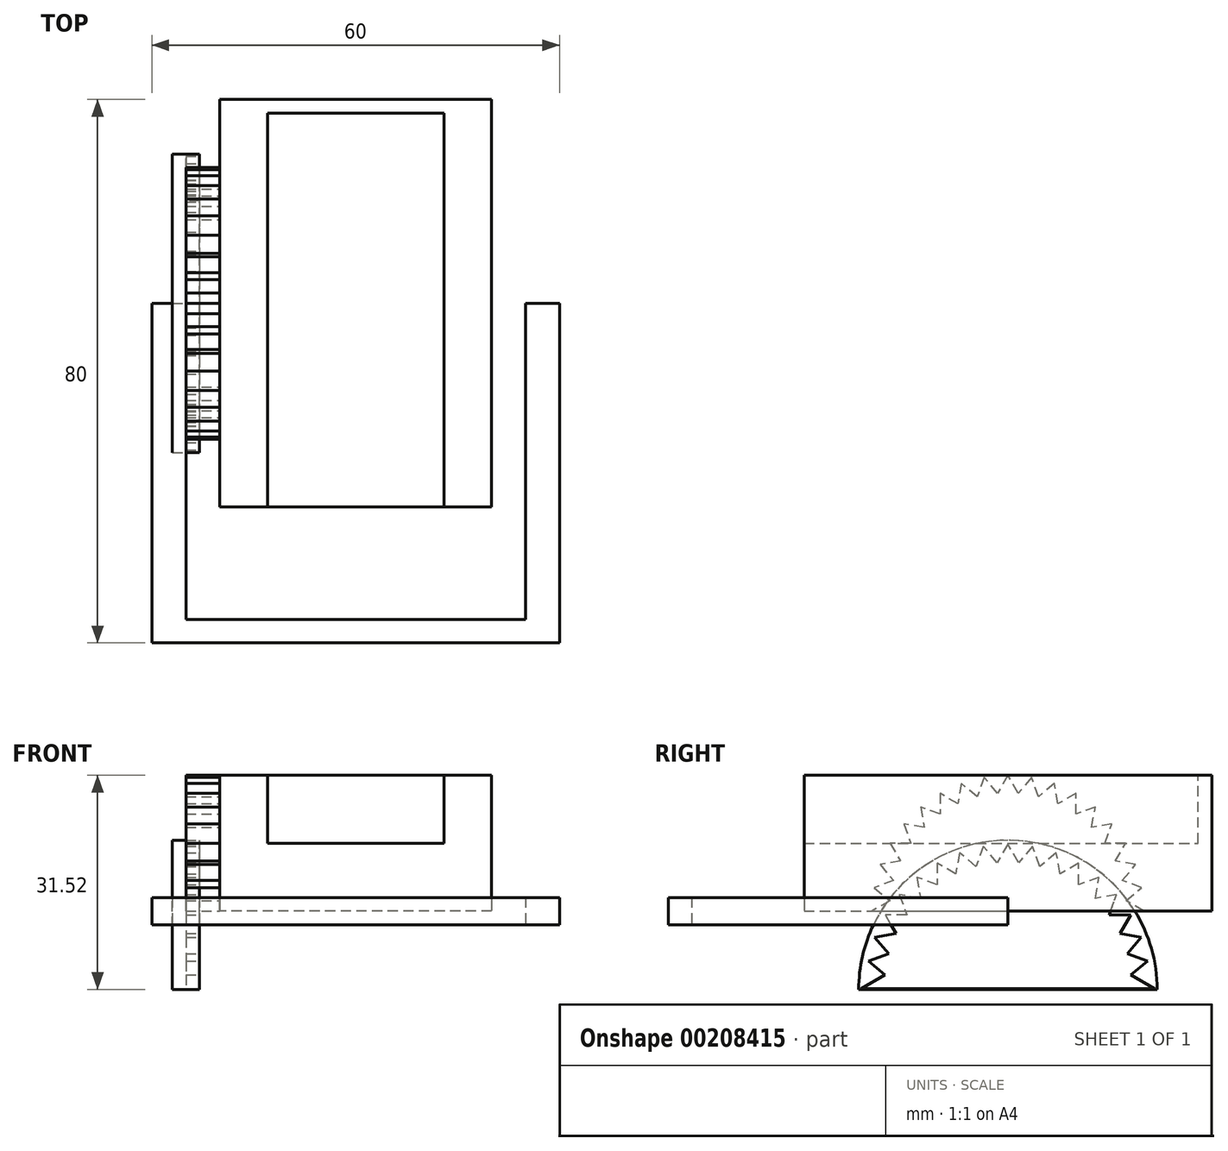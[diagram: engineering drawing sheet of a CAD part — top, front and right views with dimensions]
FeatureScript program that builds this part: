
annotation { "Feature Type Name" : "Feature", "Feature Type Description" : "" }
export const myFeature = defineFeature(function(context is Context, id is Id, definition is map)
    precondition{}
    {
        {
            var Q0;
            Q0=qCreatedBy(makeId("Top.planeOp"),FACE);
            var sketch = newSketch(context, id + "F0", { "sketchPlane" : qUnion([Q0])});
            skLineSegment(sketch, "E0.bottom", {"start": v(-20, -30) * mm, "end": v(20, -30) * mm});
            skLineSegment(sketch, "E0.top", {"start": v(-20, 30) * mm, "end": v(20, 30) * mm});
            skLineSegment(sketch, "E0.left", {"start": v(-20, -30) * mm, "end": v(-20, 30) * mm});
            skLineSegment(sketch, "E0.right", {"start": v(20, -30) * mm, "end": v(20, 30) * mm});
            skSolve(sketch);
        }
        {
            var Q0;
            Q0=qSketchRegion(id+"F0",true);
            extrude(context, id + "F1", {"entities" : qUnion([Q0]), "depth" : 20 * mm});
        }
        {
            var Q0;
            Q0=makeQuery(id+"F1.opExtrude","CAP_FACE",FACE,{"disambiguationData":[OSD([sQuery(id+"F0.wireOp",EDGE,"E0.bottom"),sQuery(id+"F0.wireOp",EDGE,"E0.top"),sQuery(id+"F0.wireOp",EDGE,"E0.left"),sQuery(id+"F0.wireOp",EDGE,"E0.right")])],"isStart":false});
            var sketch = newSketch(context, id + "F2", { "sketchPlane" : qUnion([Q0])});
            skLineSegment(sketch, "E1.top", {"start": v(-13, 28) * mm, "end": v(13, 28) * mm});
            skLineSegment(sketch, "E1.left", {"start": v(-13, -32) * mm, "end": v(-13, 28) * mm});
            skLineSegment(sketch, "E1.right", {"start": v(13, -32) * mm, "end": v(13, 28) * mm});
            skLineSegment(sketch, "E2", {"start": v(13, -32) * mm, "end": v(-13, -32) * mm});
            skSolve(sketch);
        }
        {
            var Q0;
            Q0=makeQuery(id+"F2.imprint","IMPRINT",FACE,{"disambiguationData":[TD([[makeQuery(id+"F2.imprint","IMPRINT",EDGE,{"derivedFrom":sQuery(id+"F2.wireOp",EDGE,"E1.top")}),-1.0]])]});
            extrude(context, id + "F3", {"entities" : qUnion([Q0]), "operationType" : NewBodyOperationType.REMOVE, "oppositeDirection" : true, "depth" : 10 * mm});
        }
        {
            var Q0;
            Q0=makeQuery(id+"F1.opExtrude","SWEPT_FACE",FACE,{"disambiguationData":[OSD([sQuery(id+"F0.wireOp",EDGE,"E0.right")])]});
            var sketch = newSketch(context, id + "F4", { "sketchPlane" : qUnion([Q0])});
            skPoint(sketch, "E3.center", {"position": v(0, 0) * mm});
            skLineSegment(sketch, "E4", {"start": v(7.37, 15.8) * mm, "end": v(6.84, 18.8) * mm});
            skLineSegment(sketch, "E5", {"start": v(6.84, 18.8) * mm, "end": v(4.51, 16.84) * mm});
            skLineSegment(sketch, "E6.1.0", {"start": v(4.51, 16.84) * mm, "end": v(3.47, 19.7) * mm});
            skLineSegment(sketch, "E6.1.1", {"start": v(3.47, 19.7) * mm, "end": v(1.52, 17.37) * mm});
            skLineSegment(sketch, "E6.2.0", {"start": v(1.52, 17.37) * mm, "end": v(0, 20) * mm});
            skLineSegment(sketch, "E6.2.1", {"start": v(0, 20) * mm, "end": v(-1.52, 17.37) * mm});
            skLineSegment(sketch, "E6.3.0", {"start": v(-1.52, 17.37) * mm, "end": v(-3.47, 19.7) * mm});
            skLineSegment(sketch, "E6.3.1", {"start": v(-3.47, 19.7) * mm, "end": v(-4.51, 16.84) * mm});
            skLineSegment(sketch, "E6.4.0", {"start": v(-4.51, 16.84) * mm, "end": v(-6.84, 18.8) * mm});
            skLineSegment(sketch, "E6.4.1", {"start": v(-6.84, 18.8) * mm, "end": v(-7.37, 15.8) * mm});
            skLineSegment(sketch, "E6.5.0", {"start": v(-7.37, 15.8) * mm, "end": v(-10, 17.32) * mm});
            skLineSegment(sketch, "E6.5.1", {"start": v(-10, 17.32) * mm, "end": v(-10, 14.28) * mm});
            skLineSegment(sketch, "E6.6.0", {"start": v(-10, 14.28) * mm, "end": v(-12.86, 15.32) * mm});
            skLineSegment(sketch, "E6.6.1", {"start": v(-12.86, 15.32) * mm, "end": v(-12.33, 12.33) * mm});
            skLineSegment(sketch, "E6.7.0", {"start": v(-12.33, 12.33) * mm, "end": v(-15.32, 12.86) * mm});
            skLineSegment(sketch, "E6.7.1", {"start": v(-15.32, 12.86) * mm, "end": v(-14.28, 10) * mm});
            skLineSegment(sketch, "E6.8.0", {"start": v(-14.28, 10) * mm, "end": v(-17.32, 10) * mm});
            skLineSegment(sketch, "E6.8.1", {"start": v(-17.32, 10) * mm, "end": v(-15.8, 7.37) * mm});
            skLineSegment(sketch, "E6.9.0", {"start": v(-15.8, 7.37) * mm, "end": v(-18.8, 6.84) * mm});
            skLineSegment(sketch, "E6.9.1", {"start": v(-18.8, 6.84) * mm, "end": v(-16.84, 4.51) * mm});
            skLineSegment(sketch, "E6.10.0", {"start": v(-16.84, 4.51) * mm, "end": v(-19.7, 3.47) * mm});
            skLineSegment(sketch, "E6.10.1", {"start": v(-19.7, 3.47) * mm, "end": v(-17.37, 1.52) * mm});
            skLineSegment(sketch, "E6.11.0", {"start": v(-17.37, 1.52) * mm, "end": v(-20, 0) * mm});
            skLineSegment(sketch, "E6.29.1", {"start": v(20, 0) * mm, "end": v(17.37, 1.52) * mm});
            skLineSegment(sketch, "E6.30.0", {"start": v(17.37, 1.52) * mm, "end": v(19.7, 3.47) * mm});
            skLineSegment(sketch, "E6.30.1", {"start": v(19.7, 3.47) * mm, "end": v(16.84, 4.51) * mm});
            skLineSegment(sketch, "E6.31.0", {"start": v(16.84, 4.51) * mm, "end": v(18.8, 6.84) * mm});
            skLineSegment(sketch, "E6.31.1", {"start": v(18.8, 6.84) * mm, "end": v(15.8, 7.37) * mm});
            skLineSegment(sketch, "E6.32.0", {"start": v(15.8, 7.37) * mm, "end": v(17.32, 10) * mm});
            skLineSegment(sketch, "E6.32.1", {"start": v(17.32, 10) * mm, "end": v(14.28, 10) * mm});
            skLineSegment(sketch, "E6.33.0", {"start": v(14.28, 10) * mm, "end": v(15.32, 12.86) * mm});
            skLineSegment(sketch, "E6.33.1", {"start": v(15.32, 12.86) * mm, "end": v(12.33, 12.33) * mm});
            skLineSegment(sketch, "E6.34.0", {"start": v(12.33, 12.33) * mm, "end": v(12.86, 15.32) * mm});
            skLineSegment(sketch, "E6.34.1", {"start": v(12.86, 15.32) * mm, "end": v(10, 14.28) * mm});
            skLineSegment(sketch, "E6.35.0", {"start": v(10, 14.28) * mm, "end": v(10, 17.32) * mm});
            skLineSegment(sketch, "E6.35.1", {"start": v(10, 17.32) * mm, "end": v(7.37, 15.8) * mm});
            skLineSegment(sketch, "E7", {"start": v(20, 0) * mm, "end": v(-20, 0) * mm});
            skSolve(sketch);
        }
        {
            var Q0;
            Q0=makeQuery(id+"F4.imprint","IMPRINT",FACE,{"disambiguationData":[TD([[makeQuery(id+"F4.imprint","IMPRINT",EDGE,{"derivedFrom":sQuery(id+"F4.wireOp",EDGE,"E4")}),1.0]])]});
            extrude(context, id + "F5", {"entities" : qUnion([Q0]), "operationType" : NewBodyOperationType.ADD, "depth" : 5 * mm});
        }
        {
            var Q0;
            Q0=makeQuery(id+"F1.opExtrude","SWEPT_BODY",BODY,{"disambiguationData":[OSD([sQuery(id+"F0.wireOp",EDGE,"E0.bottom"),sQuery(id+"F0.wireOp",EDGE,"E0.top"),sQuery(id+"F0.wireOp",EDGE,"E0.left"),sQuery(id+"F0.wireOp",EDGE,"E0.right")])]});
            var Q1;
            Q1=qCreatedBy(makeId("Right.planeOp"),FACE);
            mirror(context, id + "F6", {"entities" : qUnion([Q0]), "mirrorPlane" : qUnion([Q1])});
        }
        {
            var Q0;
            Q0=qCreatedBy(makeId("Right.planeOp"),FACE);
            cPlane(context, id + "F7", {"entities" : qUnion([Q0]), "cplaneType" : CPlaneType.OFFSET, "offset" : 23 * mm, "width" : 152.4 * mm, "height" : 152.4 * mm});
        }
        {
            var Q0;
            Q0=qCreatedBy(makeId("Right.planeOp"),FACE);
            cPlane(context, id + "F8", {"entities" : qUnion([Q0]), "cplaneType" : CPlaneType.OFFSET, "offset" : 23 * mm, "oppositeDirection" : true, "width" : 152.4 * mm, "height" : 152.4 * mm});
        }
        {
            var Q0;
            Q0=qCreatedBy(id+"F8.planeOp",FACE);
            var sketch = newSketch(context, id + "F9", { "sketchPlane" : qUnion([Q0])});
            skPoint(sketch, "E8.center", {"position": v(0, -11) * mm});
            skLineSegment(sketch, "E9", {"start": v(7.37, 4.81) * mm, "end": v(6.84, 7.8) * mm});
            skLineSegment(sketch, "E10", {"start": v(6.84, 7.8) * mm, "end": v(4.51, 5.85) * mm});
            skLineSegment(sketch, "E11.1.0", {"start": v(4.51, 5.85) * mm, "end": v(3.47, 8.7) * mm});
            skLineSegment(sketch, "E11.1.1", {"start": v(3.47, 8.7) * mm, "end": v(1.52, 6.38) * mm});
            skLineSegment(sketch, "E11.2.0", {"start": v(1.52, 6.38) * mm, "end": v(0, 9) * mm});
            skLineSegment(sketch, "E11.2.1", {"start": v(0, 9) * mm, "end": v(-1.52, 6.38) * mm});
            skLineSegment(sketch, "E11.3.0", {"start": v(-1.52, 6.38) * mm, "end": v(-3.47, 8.7) * mm});
            skLineSegment(sketch, "E11.3.1", {"start": v(-3.47, 8.7) * mm, "end": v(-4.51, 5.85) * mm});
            skLineSegment(sketch, "E11.4.0", {"start": v(-4.51, 5.85) * mm, "end": v(-6.84, 7.8) * mm});
            skLineSegment(sketch, "E11.4.1", {"start": v(-6.84, 7.8) * mm, "end": v(-7.37, 4.81) * mm});
            skLineSegment(sketch, "E11.5.0", {"start": v(-7.37, 4.81) * mm, "end": v(-10, 6.33) * mm});
            skLineSegment(sketch, "E11.5.1", {"start": v(-10, 6.33) * mm, "end": v(-10, 3.3) * mm});
            skLineSegment(sketch, "E11.6.0", {"start": v(-10, 3.3) * mm, "end": v(-12.86, 4.33) * mm});
            skLineSegment(sketch, "E11.6.1", {"start": v(-12.86, 4.33) * mm, "end": v(-12.33, 1.34) * mm});
            skLineSegment(sketch, "E11.7.0", {"start": v(-12.33, 1.34) * mm, "end": v(-15.32, 1.87) * mm});
            skLineSegment(sketch, "E11.7.1", {"start": v(-15.32, 1.87) * mm, "end": v(-14.28, -1) * mm});
            skLineSegment(sketch, "E11.8.0", {"start": v(-14.28, -1) * mm, "end": v(-17.32, -1) * mm});
            skLineSegment(sketch, "E11.8.1", {"start": v(-17.32, -1) * mm, "end": v(-15.8, -3.62) * mm});
            skLineSegment(sketch, "E11.9.0", {"start": v(-15.8, -3.62) * mm, "end": v(-18.8, -4.15) * mm});
            skLineSegment(sketch, "E11.9.1", {"start": v(-18.8, -4.15) * mm, "end": v(-16.84, -6.48) * mm});
            skLineSegment(sketch, "E11.10.0", {"start": v(-16.84, -6.48) * mm, "end": v(-19.7, -7.52) * mm});
            skLineSegment(sketch, "E11.10.1", {"start": v(-19.7, -7.52) * mm, "end": v(-17.37, -9.47) * mm});
            skLineSegment(sketch, "E11.11.0", {"start": v(-17.37, -9.47) * mm, "end": v(-20, -11) * mm});
            skLineSegment(sketch, "E11.29.1", {"start": v(20, -11) * mm, "end": v(17.37, -9.47) * mm});
            skLineSegment(sketch, "E11.30.0", {"start": v(17.37, -9.47) * mm, "end": v(19.7, -7.52) * mm});
            skLineSegment(sketch, "E11.30.1", {"start": v(19.7, -7.52) * mm, "end": v(16.84, -6.48) * mm});
            skLineSegment(sketch, "E11.31.0", {"start": v(16.84, -6.48) * mm, "end": v(18.8, -4.15) * mm});
            skLineSegment(sketch, "E11.31.1", {"start": v(18.8, -4.15) * mm, "end": v(15.8, -3.62) * mm});
            skLineSegment(sketch, "E11.32.0", {"start": v(15.8, -3.62) * mm, "end": v(17.32, -1) * mm});
            skLineSegment(sketch, "E11.32.1", {"start": v(17.32, -1) * mm, "end": v(14.28, -1) * mm});
            skLineSegment(sketch, "E11.33.0", {"start": v(14.28, -1) * mm, "end": v(15.32, 1.87) * mm});
            skLineSegment(sketch, "E11.33.1", {"start": v(15.32, 1.87) * mm, "end": v(12.33, 1.34) * mm});
            skLineSegment(sketch, "E11.34.0", {"start": v(12.33, 1.34) * mm, "end": v(12.86, 4.33) * mm});
            skLineSegment(sketch, "E11.34.1", {"start": v(12.86, 4.33) * mm, "end": v(10, 3.3) * mm});
            skLineSegment(sketch, "E11.35.0", {"start": v(10, 3.3) * mm, "end": v(10, 6.33) * mm});
            skLineSegment(sketch, "E11.35.1", {"start": v(10, 6.33) * mm, "end": v(7.37, 4.81) * mm});
            skLineSegment(sketch, "E12", {"start": v(20, -11) * mm, "end": v(-20, -11) * mm});
            skSolve(sketch);
        }
        {
            var Q0;
            Q0=qCreatedBy(id+"F8.planeOp",FACE);
            var sketch = newSketch(context, id + "F10", { "sketchPlane" : qUnion([Q0])});
            skLineSegment(sketch, "E13.0", {"start": v(10.43, 3.9) * mm, "end": v(10.43, 7.08) * mm});
            skLineSegment(sketch, "E13.1", {"start": v(13.41, 5) * mm, "end": v(10.43, 3.9) * mm});
            skLineSegment(sketch, "E13.2", {"start": v(12.86, 1.87) * mm, "end": v(13.41, 5) * mm});
            skLineSegment(sketch, "E13.3", {"start": v(15.98, 2.42) * mm, "end": v(12.86, 1.87) * mm});
            skLineSegment(sketch, "E13.4", {"start": v(14.9, -0.56) * mm, "end": v(15.98, 2.42) * mm});
            skLineSegment(sketch, "E13.5", {"start": v(18.07, -0.56) * mm, "end": v(14.9, -0.56) * mm});
            skLineSegment(sketch, "E13.6", {"start": v(16.48, -3.3) * mm, "end": v(18.07, -0.56) * mm});
            skLineSegment(sketch, "E13.7", {"start": v(19.6, -3.85) * mm, "end": v(16.48, -3.3) * mm});
            skLineSegment(sketch, "E13.8", {"start": v(17.57, -6.28) * mm, "end": v(19.6, -3.85) * mm});
            skLineSegment(sketch, "E13.9", {"start": v(20.55, -7.37) * mm, "end": v(17.57, -6.28) * mm});
            skLineSegment(sketch, "E13.10", {"start": v(18.12, -9.4) * mm, "end": v(20.55, -7.37) * mm});
            skLineSegment(sketch, "E13.11", {"start": v(10.43, 7.08) * mm, "end": v(7.69, 5.5) * mm});
            skLineSegment(sketch, "E13.12", {"start": v(21.61, -11.42) * mm, "end": v(18.12, -9.4) * mm});
            skLineSegment(sketch, "E13.13", {"start": v(-21.61, -11.42) * mm, "end": v(21.61, -11.42) * mm});
            skLineSegment(sketch, "E13.14", {"start": v(-18.12, -9.4) * mm, "end": v(-21.61, -11.42) * mm});
            skLineSegment(sketch, "E13.15", {"start": v(-7.14, 8.61) * mm, "end": v(-7.69, 5.5) * mm});
            skLineSegment(sketch, "E13.16", {"start": v(-4.7, 6.58) * mm, "end": v(-7.14, 8.61) * mm});
            skLineSegment(sketch, "E13.17", {"start": v(-3.62, 9.56) * mm, "end": v(-4.7, 6.58) * mm});
            skLineSegment(sketch, "E13.18", {"start": v(-1.59, 7.13) * mm, "end": v(-3.62, 9.56) * mm});
            skLineSegment(sketch, "E13.19", {"start": v(0, 9.87) * mm, "end": v(-1.59, 7.13) * mm});
            skLineSegment(sketch, "E13.20", {"start": v(1.59, 7.13) * mm, "end": v(0, 9.87) * mm});
            skLineSegment(sketch, "E13.21", {"start": v(7.69, 5.5) * mm, "end": v(7.14, 8.61) * mm});
            skLineSegment(sketch, "E13.22", {"start": v(7.14, 8.61) * mm, "end": v(4.7, 6.58) * mm});
            skLineSegment(sketch, "E13.23", {"start": v(4.7, 6.58) * mm, "end": v(3.62, 9.56) * mm});
            skLineSegment(sketch, "E13.24", {"start": v(3.62, 9.56) * mm, "end": v(1.59, 7.13) * mm});
            skLineSegment(sketch, "E13.25", {"start": v(-7.69, 5.5) * mm, "end": v(-10.43, 7.08) * mm});
            skLineSegment(sketch, "E13.26", {"start": v(-10.43, 7.08) * mm, "end": v(-10.43, 3.9) * mm});
            skLineSegment(sketch, "E13.27", {"start": v(-10.43, 3.9) * mm, "end": v(-13.41, 5) * mm});
            skLineSegment(sketch, "E13.28", {"start": v(-13.41, 5) * mm, "end": v(-12.86, 1.87) * mm});
            skLineSegment(sketch, "E13.29", {"start": v(-12.86, 1.87) * mm, "end": v(-15.98, 2.42) * mm});
            skLineSegment(sketch, "E13.30", {"start": v(-15.98, 2.42) * mm, "end": v(-14.9, -0.56) * mm});
            skLineSegment(sketch, "E13.31", {"start": v(-14.9, -0.56) * mm, "end": v(-18.07, -0.56) * mm});
            skLineSegment(sketch, "E13.32", {"start": v(-18.07, -0.56) * mm, "end": v(-16.48, -3.3) * mm});
            skLineSegment(sketch, "E13.33", {"start": v(-16.48, -3.3) * mm, "end": v(-19.6, -3.85) * mm});
            skLineSegment(sketch, "E13.34", {"start": v(-19.6, -3.85) * mm, "end": v(-17.57, -6.28) * mm});
            skLineSegment(sketch, "E13.35", {"start": v(-17.57, -6.28) * mm, "end": v(-20.55, -7.37) * mm});
            skLineSegment(sketch, "E13.36", {"start": v(-20.55, -7.37) * mm, "end": v(-18.12, -9.4) * mm});
            skSolve(sketch);
        }
        {
            var Q0;
            Q0=qCreatedBy(id+"F7.planeOp",FACE);
            var sketch = newSketch(context, id + "F11", { "sketchPlane" : qUnion([Q0])});
            skLineSegment(sketch, "E14.0", {"start": v(10.43, 3.98) * mm, "end": v(10.43, 7.15) * mm});
            skLineSegment(sketch, "E14.1", {"start": v(13.41, 5.06) * mm, "end": v(10.43, 3.98) * mm});
            skLineSegment(sketch, "E14.2", {"start": v(12.86, 1.94) * mm, "end": v(13.41, 5.06) * mm});
            skLineSegment(sketch, "E14.3", {"start": v(15.98, 2.5) * mm, "end": v(12.86, 1.94) * mm});
            skLineSegment(sketch, "E14.4", {"start": v(14.9, -0.49) * mm, "end": v(15.98, 2.5) * mm});
            skLineSegment(sketch, "E14.5", {"start": v(18.07, -0.49) * mm, "end": v(14.9, -0.49) * mm});
            skLineSegment(sketch, "E14.6", {"start": v(16.48, -3.23) * mm, "end": v(18.07, -0.49) * mm});
            skLineSegment(sketch, "E14.7", {"start": v(19.6, -3.78) * mm, "end": v(16.48, -3.23) * mm});
            skLineSegment(sketch, "E14.8", {"start": v(17.57, -6.21) * mm, "end": v(19.6, -3.78) * mm});
            skLineSegment(sketch, "E14.9", {"start": v(20.55, -7.3) * mm, "end": v(17.57, -6.21) * mm});
            skLineSegment(sketch, "E14.10", {"start": v(18.12, -9.33) * mm, "end": v(20.55, -7.3) * mm});
            skLineSegment(sketch, "E14.11", {"start": v(10.43, 7.15) * mm, "end": v(7.69, 5.57) * mm});
            skLineSegment(sketch, "E14.12", {"start": v(21.61, -11.35) * mm, "end": v(18.12, -9.33) * mm});
            skLineSegment(sketch, "E14.13", {"start": v(-21.61, -11.35) * mm, "end": v(21.61, -11.35) * mm});
            skLineSegment(sketch, "E14.14", {"start": v(-18.12, -9.33) * mm, "end": v(-21.61, -11.35) * mm});
            skLineSegment(sketch, "E14.15", {"start": v(-7.14, 8.69) * mm, "end": v(-7.69, 5.57) * mm});
            skLineSegment(sketch, "E14.16", {"start": v(-4.7, 6.65) * mm, "end": v(-7.14, 8.69) * mm});
            skLineSegment(sketch, "E14.17", {"start": v(-3.62, 9.63) * mm, "end": v(-4.7, 6.65) * mm});
            skLineSegment(sketch, "E14.18", {"start": v(-1.59, 7.2) * mm, "end": v(-3.62, 9.63) * mm});
            skLineSegment(sketch, "E14.19", {"start": v(0, 9.95) * mm, "end": v(-1.59, 7.2) * mm});
            skLineSegment(sketch, "E14.20", {"start": v(1.59, 7.2) * mm, "end": v(0, 9.95) * mm});
            skLineSegment(sketch, "E14.21", {"start": v(7.69, 5.57) * mm, "end": v(7.14, 8.69) * mm});
            skLineSegment(sketch, "E14.22", {"start": v(7.14, 8.69) * mm, "end": v(4.7, 6.65) * mm});
            skLineSegment(sketch, "E14.23", {"start": v(4.7, 6.65) * mm, "end": v(3.62, 9.63) * mm});
            skLineSegment(sketch, "E14.24", {"start": v(3.62, 9.63) * mm, "end": v(1.59, 7.2) * mm});
            skLineSegment(sketch, "E14.25", {"start": v(-7.69, 5.57) * mm, "end": v(-10.43, 7.15) * mm});
            skLineSegment(sketch, "E14.26", {"start": v(-10.43, 7.15) * mm, "end": v(-10.43, 3.98) * mm});
            skLineSegment(sketch, "E14.27", {"start": v(-10.43, 3.98) * mm, "end": v(-13.41, 5.06) * mm});
            skLineSegment(sketch, "E14.28", {"start": v(-13.41, 5.06) * mm, "end": v(-12.86, 1.94) * mm});
            skLineSegment(sketch, "E14.29", {"start": v(-12.86, 1.94) * mm, "end": v(-15.98, 2.5) * mm});
            skLineSegment(sketch, "E14.30", {"start": v(-15.98, 2.5) * mm, "end": v(-14.9, -0.49) * mm});
            skLineSegment(sketch, "E14.31", {"start": v(-14.9, -0.49) * mm, "end": v(-18.07, -0.49) * mm});
            skLineSegment(sketch, "E14.32", {"start": v(-18.07, -0.49) * mm, "end": v(-16.48, -3.23) * mm});
            skLineSegment(sketch, "E14.33", {"start": v(-16.48, -3.23) * mm, "end": v(-19.6, -3.78) * mm});
            skLineSegment(sketch, "E14.34", {"start": v(-19.6, -3.78) * mm, "end": v(-17.57, -6.21) * mm});
            skLineSegment(sketch, "E14.35", {"start": v(-17.57, -6.21) * mm, "end": v(-20.55, -7.3) * mm});
            skLineSegment(sketch, "E14.36", {"start": v(-20.55, -7.3) * mm, "end": v(-18.12, -9.33) * mm});
            skSolve(sketch);
        }
        {
            var Q0;
            Q0=qCreatedBy(id+"F8.planeOp",FACE);
            var sketch = newSketch(context, id + "F12", { "sketchPlane" : qUnion([Q0])});
            skArc(sketch, "E15", {"start": v(21.96, -11.52) * mm, "mid": v(0, 10.44) * mm, "end": v(-21.96, -11.52) * mm});
            skLineSegment(sketch, "E16", {"start": v(21.96, -11.52) * mm, "end": v(-21.96, -11.52) * mm});
            skPoint(sketch, "E17.orphan", {"position": v(23.52, -11.52) * mm});
            skSolve(sketch);
        }
        {
            var Q0;
            Q0=qCreatedBy(id+"F7.planeOp",FACE);
            var sketch = newSketch(context, id + "F13", { "sketchPlane" : qUnion([Q0])});
            skArc(sketch, "E18", {"start": v(21.96, -11.52) * mm, "mid": v(0, 10.44) * mm, "end": v(-21.96, -11.52) * mm});
            skLineSegment(sketch, "E19", {"start": v(21.96, -11.52) * mm, "end": v(-21.96, -11.52) * mm});
            skPoint(sketch, "E20.orphan", {"position": v(23.52, -11.52) * mm});
            skSolve(sketch);
        }
        {
            var Q0;
            Q0 = qSketchRegion(id + "F12", true);
            extrude(context, id + "F14", {"entities" : qUnion([Q0]), "oppositeDirection" : true, "depth" : 4 * mm});
        }
        {
            var Q0;
            Q0 = qSketchRegion(id + "F10", true);
            extrude(context, id + "F15", {"entities" : qUnion([Q0]), "operationType" : NewBodyOperationType.REMOVE, "oppositeDirection" : true, "depth" : 2 * mm});
        }
        {
            var Q0;
            Q0 = qSketchRegion(id + "F13", true);
            extrude(context, id + "F16", {"entities" : qUnion([Q0]), "operationType" : NewBodyOperationType.ADD, "depth" : 4 * mm});
        }
        {
            var Q0;
            Q0 = qSketchRegion(id + "F11", true);
            extrude(context, id + "F17", {"entities" : qUnion([Q0]), "operationType" : NewBodyOperationType.REMOVE, "depth" : 2 * mm});
        }
        {
            var Q0;
            Q0=makeQuery(id+"F1.opExtrude","SWEPT_BODY",BODY,{"disambiguationData":[OSD([sQuery(id+"F0.wireOp",EDGE,"E0.bottom"),sQuery(id+"F0.wireOp",EDGE,"E0.top"),sQuery(id+"F0.wireOp",EDGE,"E0.left"),sQuery(id+"F0.wireOp",EDGE,"E0.right")])]});
            deleteBodies(context, id + "F18", {"entities" : qUnion([Q0])});
        }
        {
            var Q0;
            Q0=qCreatedBy(makeId("Top.planeOp"),FACE);
            var sketch = newSketch(context, id + "F19", { "sketchPlane" : qUnion([Q0])});
            skLineSegment(sketch, "E21.bottom", {"start": v(-30, 0) * mm, "end": v(-25, 0) * mm});
            skLineSegment(sketch, "E21.top", {"start": v(-30, -50) * mm, "end": v(30, -50) * mm});
            skLineSegment(sketch, "E21.left", {"start": v(-30, 0) * mm, "end": v(-30, -50) * mm});
            skLineSegment(sketch, "E21.right", {"start": v(30, 0) * mm, "end": v(30, -50) * mm});
            skLineSegment(sketch, "E22.top", {"start": v(-25, -46.55) * mm, "end": v(25, -46.55) * mm});
            skLineSegment(sketch, "E22.left", {"start": v(-25, 0) * mm, "end": v(-25, -46.55) * mm});
            skLineSegment(sketch, "E22.right", {"start": v(25, 0) * mm, "end": v(25, -46.55) * mm});
            skLineSegment(sketch, "E23.trimOffspring", {"start": v(25, 0) * mm, "end": v(30, 0) * mm});
            skSolve(sketch);
        }
        {
            var Q0;
            Q0 = qSketchRegion(id + "F19", true);
            extrude(context, id + "F20", {"entities" : qUnion([Q0]), "endBound" : BoundingType.SYMMETRIC, "depth" : 4 * mm});
        }
    });
